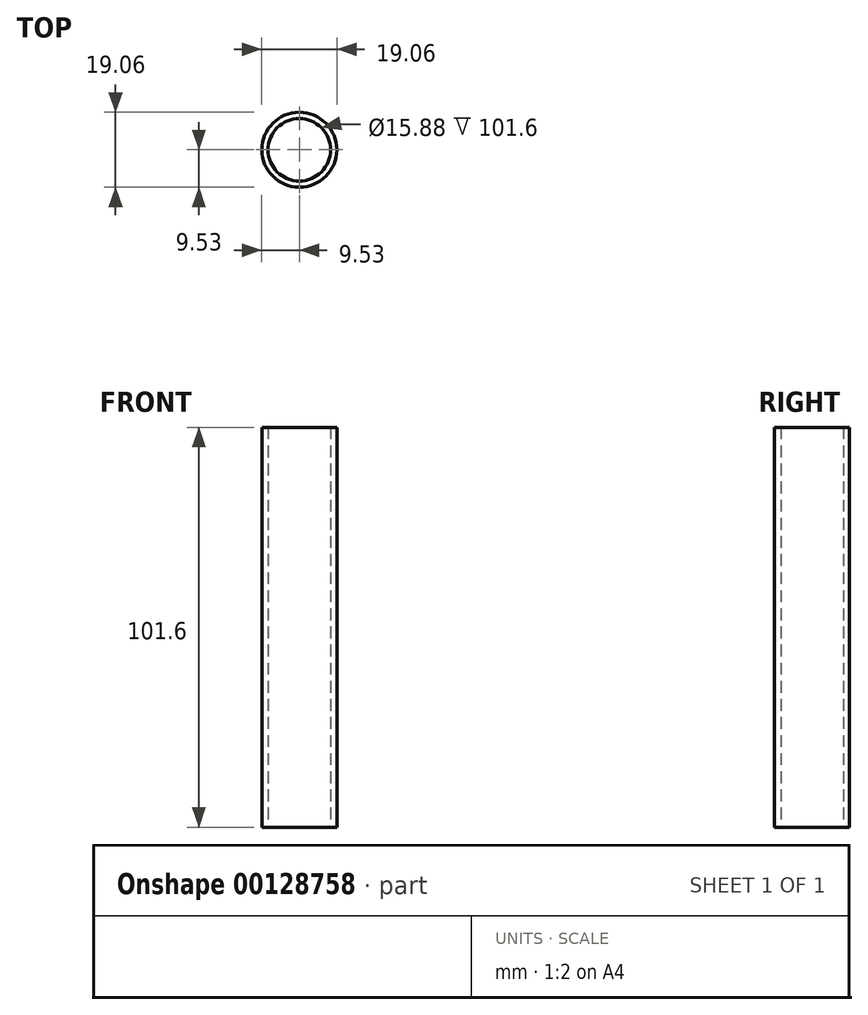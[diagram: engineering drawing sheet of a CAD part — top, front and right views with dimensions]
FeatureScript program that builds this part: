
annotation { "Feature Type Name" : "Feature", "Feature Type Description" : "" }
export const myFeature = defineFeature(function(context is Context, id is Id, definition is map)
    precondition{}
    {
        {
            var Q0;
            Q0=qCreatedBy(makeId("Top.planeOp"),FACE);
            var sketch = newSketch(context, id + "F0", { "sketchPlane" : qUnion([Q0])});
            skCircle(sketch, "E0", {"center": v(0, 0) * mm, "radius": 9.53 * mm});
            skCircle(sketch, "E1", {"center": v(0, 0) * mm, "radius": 7.94 * mm});
            skSolve(sketch);
        }
        {
            var Q0;
            Q0=makeQuery(id+"F0.imprint","IMPRINT",FACE,{"disambiguationData":[TD([[makeQuery(id+"F0.imprint","IMPRINT",EDGE,{"derivedFrom":sQuery(id+"F0.wireOp",EDGE,"E0")}),1.0]])]});
            extrude(context, id + "F1", {"entities" : qUnion([Q0]), "depth" : 101.6 * mm});
        }
    });
